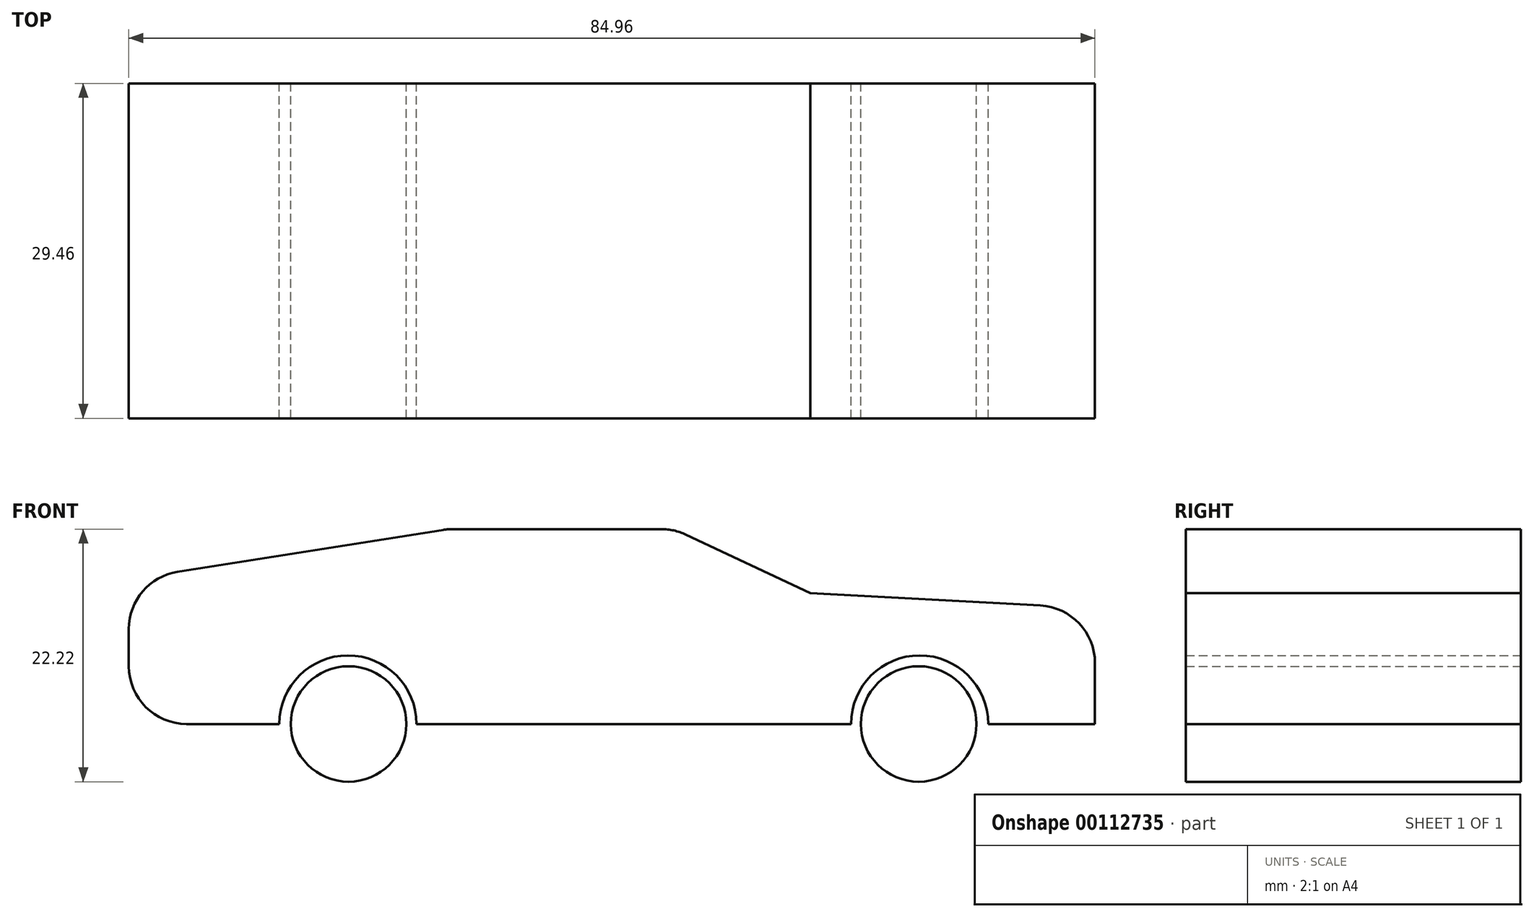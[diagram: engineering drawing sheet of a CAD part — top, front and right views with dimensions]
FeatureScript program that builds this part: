
annotation { "Feature Type Name" : "Feature", "Feature Type Description" : "" }
export const myFeature = defineFeature(function(context is Context, id is Id, definition is map)
    precondition{}
    {
        {
            var Q0;
            Q0=qCreatedBy(makeId("Front.planeOp"),FACE);
            var sketch = newSketch(context, id + "F0", { "sketchPlane" : qUnion([Q0])});
            skLineSegment(sketch, "E0.bottom", {"start": v(-41.63, 0) * mm, "end": v(-28.4, 0) * mm});
            skLineSegment(sketch, "E0.top", {"start": v(-13.56, 17.15) * mm, "end": v(6.33, 17.15) * mm});
            skLineSegment(sketch, "E0.left", {"start": v(-41.63, 0) * mm, "end": v(-41.63, 12.7) * mm});
            skLineSegment(sketch, "E0.right", {"start": v(43.33, 0) * mm, "end": v(43.33, 10.16) * mm});
            skArc(sketch, "E1", {"start": v(-16.33, 0) * mm, "mid": v(-22.36, 6.03) * mm, "end": v(-28.4, 0) * mm});
            skArc(sketch, "E2", {"start": v(33.95, 0) * mm, "mid": v(27.92, 6.03) * mm, "end": v(21.89, 0) * mm});
            skLineSegment(sketch, "E3", {"start": v(-41.63, 12.7) * mm, "end": v(-13.56, 17.15) * mm});
            skLineSegment(sketch, "E4", {"start": v(43.33, 10.16) * mm, "end": v(18.3, 11.53) * mm});
            skLineSegment(sketch, "E5", {"start": v(18.3, 11.53) * mm, "end": v(6.33, 17.15) * mm});
            skLineSegment(sketch, "E6.trimOffspring", {"start": v(-16.33, 0) * mm, "end": v(21.89, 0) * mm});
            skLineSegment(sketch, "E7.trimOffspring", {"start": v(33.95, 0) * mm, "end": v(43.33, 0) * mm});
            skSolve(sketch);
        }
        {
            var Q0;
            Q0 = qSketchRegion(id + "F0", true);
            extrude(context, id + "F1", {"entities" : qUnion([Q0]), "depth" : 29.46 * mm, "symmetric" : true});
        }
        {
            var Q0;
            Q0=qCreatedBy(makeId("Front.planeOp"),FACE);
            var sketch = newSketch(context, id + "F2", { "sketchPlane" : qUnion([Q0])});
            skCircle(sketch, "E8", {"center": v(-22.3, 0) * mm, "radius": 5.08 * mm});
            skCircle(sketch, "E9", {"center": v(27.83, 0) * mm, "radius": 5.08 * mm});
            skSolve(sketch);
        }
        {
            var Q0;
            Q0 = qSketchRegion(id + "F2", true);
            extrude(context, id + "F3", {"entities" : qUnion([Q0]), "operationType" : NewBodyOperationType.ADD, "depth" : 29.46 * mm, "symmetric" : true});
        }
        {
            var Q0;
            Q0=makeQuery(id+"F1.opExtrude","SWEPT_EDGE",EDGE,{"disambiguationData":[OSD([sQuery(id+"F0.wireOp",EDGE,"E0.left"),sQuery(id+"F0.wireOp",EDGE,"E3")])]});
            var Q1;
            Q1=makeQuery(id+"F1.opExtrude","SWEPT_EDGE",EDGE,{"disambiguationData":[OSD([sQuery(id+"F0.wireOp",EDGE,"E0.right"),sQuery(id+"F0.wireOp",EDGE,"E4")])]});
            var Q2;
            Q2=makeQuery(id+"F1.opExtrude","SWEPT_EDGE",EDGE,{"disambiguationData":[OSD([sQuery(id+"F0.wireOp",EDGE,"E0.top"),sQuery(id+"F0.wireOp",EDGE,"E5")])]});
            var Q3;
            Q3=makeQuery(id+"F1.opExtrude","SWEPT_EDGE",EDGE,{"disambiguationData":[OSD([sQuery(id+"F0.wireOp",EDGE,"E0.top"),sQuery(id+"F0.wireOp",EDGE,"E3")])]});
            var Q4;
            Q4=makeQuery(id+"F1.opExtrude","SWEPT_EDGE",EDGE,{"disambiguationData":[OSD([sQuery(id+"F0.wireOp",EDGE,"E0.bottom"),sQuery(id+"F0.wireOp",EDGE,"E0.left")])]});
            fillet(context, id + "F4", {"entities" : qUnion([Q0, Q1, Q2, Q3, Q4]), "radius" : 5.08 * mm, "tangentPropagation" : true, "allowEdgeOverflow" : false});
        }
    });
